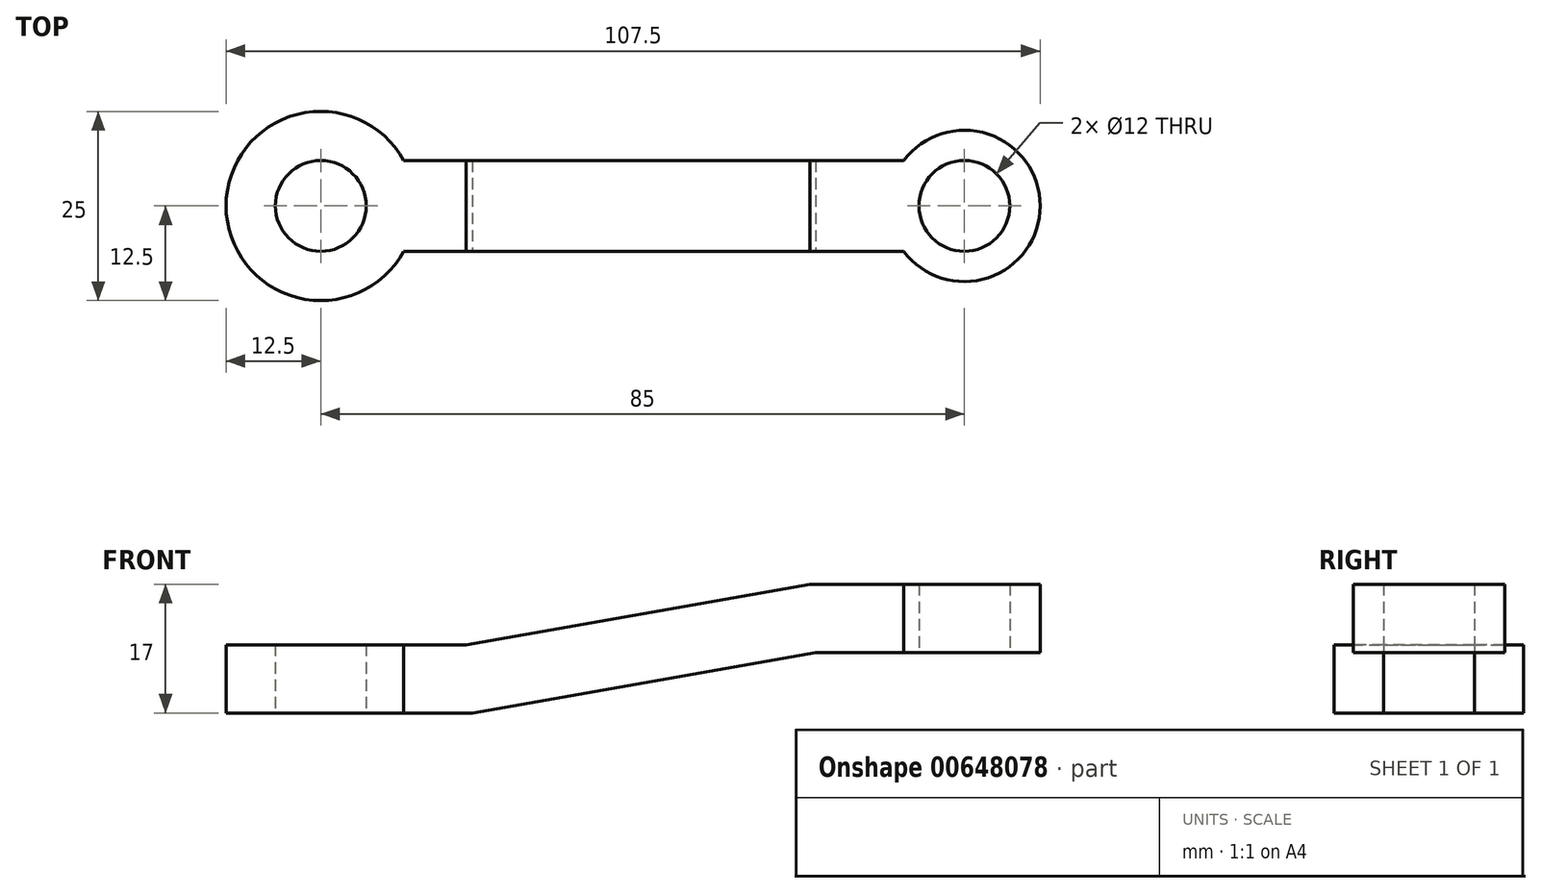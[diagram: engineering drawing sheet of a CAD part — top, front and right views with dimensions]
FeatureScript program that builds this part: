
annotation { "Feature Type Name" : "Feature", "Feature Type Description" : "" }
export const myFeature = defineFeature(function(context is Context, id is Id, definition is map)
    precondition{}
    {
        {
            var Q0;
            Q0=qCreatedBy(makeId("Top.planeOp"),FACE);
            var sketch = newSketch(context, id + "F0", { "sketchPlane" : qUnion([Q0])});
            skCircle(sketch, "E0", {"center": v(0, 0) * mm, "radius": 12.5 * mm});
            skCircle(sketch, "E1", {"center": v(85, 0) * mm, "radius": 10 * mm});
            skLineSegment(sketch, "E2", {"start": v(10.97, 6) * mm, "end": v(77, 6) * mm});
            skLineSegment(sketch, "E3", {"start": v(0, 0) * mm, "end": v(85, 0) * mm, "construction": true});
            skLineSegment(sketch, "E4.MirrorCS", {"start": v(10.97, -6) * mm, "end": v(77, -6) * mm});
            skCircle(sketch, "E5", {"center": v(0, 0) * mm, "radius": 6 * mm});
            skCircle(sketch, "E6", {"center": v(85, 0) * mm, "radius": 6 * mm});
            skSolve(sketch);
        }
        {
            var Q0;
            {var subQ0=sQuery(id+"F0.wireOp",EDGE,"E2");Q0=makeQuery(id+"F0.imprint","IMPRINT",FACE,{"disambiguationData":[TD([[makeQuery(id+"F0.imprint","IMPRINT",EDGE,{"derivedFrom":subQ0}),-1.0]])]});}
            var Q1;
            Q1=makeQuery(id+"F0.imprint","IMPRINT",FACE,{"disambiguationData":[TD([[makeQuery(id+"F0.imprint","IMPRINT",EDGE,{"derivedFrom":sQuery(id+"F0.wireOp",EDGE,"E5")}),-1.0]])]});
            var Q2;
            Q2=makeQuery(id+"F0.imprint","IMPRINT",FACE,{"disambiguationData":[TD([[makeQuery(id+"F0.imprint","IMPRINT",EDGE,{"derivedFrom":sQuery(id+"F0.wireOp",EDGE,"E6")}),-1.0]])]});
            extrude(context, id + "F1", {"entities" : qUnion([Q0, Q1, Q2]), "depth" : 25 * mm, "offsetDistance" : 25 * mm});
        }
        {
            var Q0;
            Q0=qCreatedBy(makeId("Front.planeOp"),FACE);
            var sketch = newSketch(context, id + "F2", { "sketchPlane" : qUnion([Q0])});
            skLineSegment(sketch, "E7", {"start": v(-12.5, 0) * mm, "end": v(20, 0) * mm});
            skLineSegment(sketch, "E8", {"start": v(20, 0) * mm, "end": v(65.37, 8) * mm});
            skLineSegment(sketch, "E9", {"start": v(65.37, 8) * mm, "end": v(95, 8) * mm});
            skLineSegment(sketch, "E10.0", {"start": v(64.58, 17) * mm, "end": v(95, 17) * mm});
            skLineSegment(sketch, "E10.1", {"start": v(19.21, 9) * mm, "end": v(64.58, 17) * mm});
            skLineSegment(sketch, "E10.2", {"start": v(-12.5, 9) * mm, "end": v(19.21, 9) * mm});
            skLineSegment(sketch, "E11", {"start": v(-12.5, 9) * mm, "end": v(-12.5, 0) * mm});
            skLineSegment(sketch, "E12", {"start": v(95, 17) * mm, "end": v(95, 8) * mm});
            skLineSegment(sketch, "E13", {"start": v(-12.5, 0) * mm, "end": v(-12.5, 25) * mm});
            skLineSegment(sketch, "E14", {"start": v(95, 25) * mm, "end": v(95, 0) * mm});
            skSolve(sketch);
        }
        {
            var Q0;
            Q0 = qSketchRegion(id + "F2", true);
            extrude(context, id + "F3", {"entities" : qUnion([Q0]), "operationType" : NewBodyOperationType.INTERSECT, "endBound" : BoundingType.SYMMETRIC, "oppositeDirection" : true, "depth" : 25 * mm, "offsetDistance" : 25 * mm});
        }
    });
